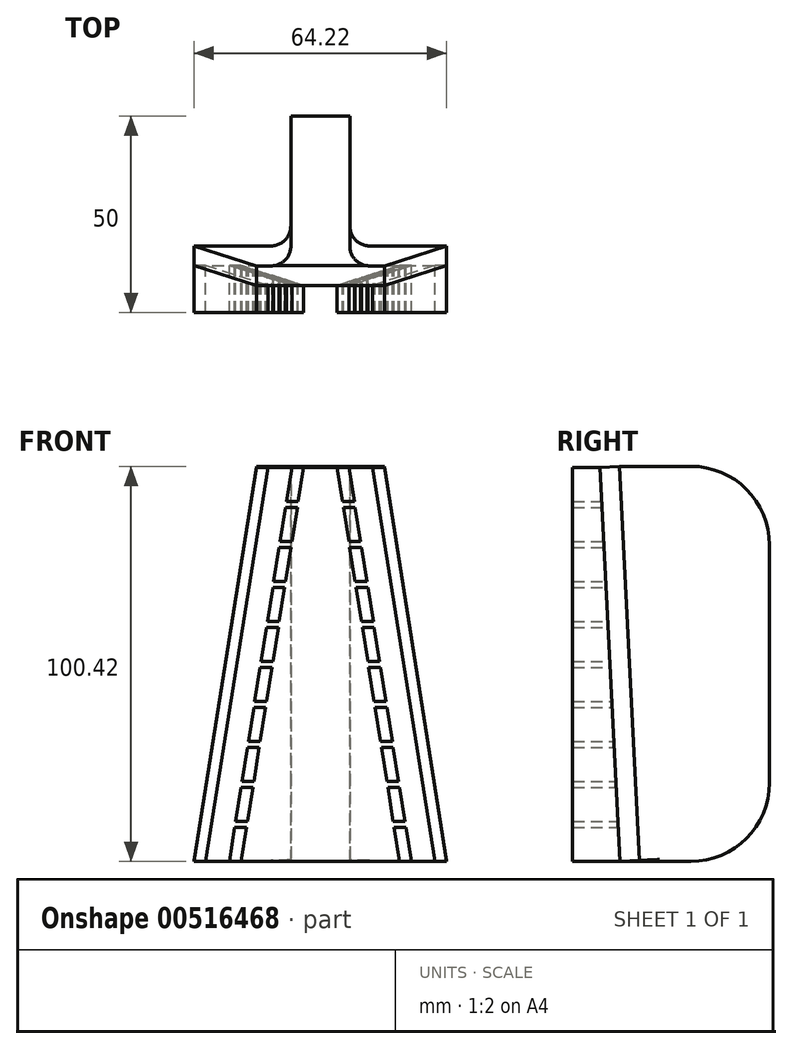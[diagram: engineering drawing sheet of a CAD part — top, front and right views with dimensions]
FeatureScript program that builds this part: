
annotation { "Feature Type Name" : "Feature", "Feature Type Description" : "" }
export const myFeature = defineFeature(function(context is Context, id is Id, definition is map)
    precondition{}
    {
        {
            var Q0;
            Q0=qCreatedBy(makeId("Front.planeOp"),FACE);
            var sketch = newSketch(context, id + "F0", { "sketchPlane" : qUnion([Q0])});
            skLineSegment(sketch, "E0", {"start": v(-21.74, 8.67) * mm, "end": v(-18.74, 8.67) * mm});
            skLineSegment(sketch, "E1", {"start": v(-18.74, 8.67) * mm, "end": v(-20.11, 0) * mm});
            skLineSegment(sketch, "E2", {"start": v(-20.11, 0) * mm, "end": v(-23.11, 0) * mm});
            skLineSegment(sketch, "E3", {"start": v(-23.11, 0) * mm, "end": v(-21.74, 8.67) * mm});
            skLineSegment(sketch, "E4", {"start": v(18.74, 8.67) * mm, "end": v(21.74, 8.67) * mm});
            skLineSegment(sketch, "E5", {"start": v(21.74, 8.67) * mm, "end": v(23.11, 0) * mm});
            skLineSegment(sketch, "E6", {"start": v(23.11, 0) * mm, "end": v(20.11, 0) * mm});
            skLineSegment(sketch, "E7", {"start": v(20.11, 0) * mm, "end": v(18.74, 8.67) * mm});
            skLineSegment(sketch, "E8", {"start": v(-21.5, 10.17) * mm, "end": v(-18.5, 10.17) * mm});
            skLineSegment(sketch, "E9", {"start": v(-18.5, 10.17) * mm, "end": v(-17.13, 18.83) * mm});
            skLineSegment(sketch, "E10", {"start": v(-17.13, 18.83) * mm, "end": v(-20.13, 18.83) * mm});
            skLineSegment(sketch, "E11", {"start": v(-20.13, 18.83) * mm, "end": v(-21.5, 10.17) * mm});
            skLineSegment(sketch, "E12", {"start": v(18.5, 10.17) * mm, "end": v(17.13, 18.83) * mm});
            skLineSegment(sketch, "E13", {"start": v(17.13, 18.83) * mm, "end": v(20.13, 18.83) * mm});
            skLineSegment(sketch, "E14", {"start": v(20.13, 18.83) * mm, "end": v(21.5, 10.17) * mm});
            skLineSegment(sketch, "E15", {"start": v(21.5, 10.17) * mm, "end": v(18.5, 10.17) * mm});
            skLineSegment(sketch, "E16", {"start": v(-18.52, 29) * mm, "end": v(-19.89, 20.33) * mm});
            skLineSegment(sketch, "E17", {"start": v(-19.89, 20.33) * mm, "end": v(-16.89, 20.33) * mm});
            skLineSegment(sketch, "E18", {"start": v(-16.89, 20.33) * mm, "end": v(-15.52, 29) * mm});
            skLineSegment(sketch, "E19", {"start": v(-15.52, 29) * mm, "end": v(-18.52, 29) * mm});
            skLineSegment(sketch, "E20", {"start": v(19.89, 20.33) * mm, "end": v(18.52, 29) * mm});
            skLineSegment(sketch, "E21", {"start": v(18.52, 29) * mm, "end": v(15.52, 29) * mm});
            skLineSegment(sketch, "E22", {"start": v(15.52, 29) * mm, "end": v(16.89, 20.33) * mm});
            skLineSegment(sketch, "E23", {"start": v(16.89, 20.33) * mm, "end": v(19.89, 20.33) * mm});
            skLineSegment(sketch, "E24", {"start": v(-16.67, 40.67) * mm, "end": v(-13.67, 40.67) * mm});
            skLineSegment(sketch, "E25", {"start": v(-13.67, 40.67) * mm, "end": v(-12.3, 49.33) * mm});
            skLineSegment(sketch, "E26", {"start": v(-12.3, 49.33) * mm, "end": v(-15.3, 49.33) * mm});
            skLineSegment(sketch, "E27", {"start": v(-15.3, 49.33) * mm, "end": v(-16.67, 40.67) * mm});
            skLineSegment(sketch, "E28", {"start": v(-13.69, 59.5) * mm, "end": v(-15.06, 50.83) * mm});
            skLineSegment(sketch, "E29", {"start": v(-8.84, 71.17) * mm, "end": v(-11.84, 71.17) * mm});
            skLineSegment(sketch, "E30", {"start": v(-7.47, 79.83) * mm, "end": v(-10.47, 79.83) * mm});
            skLineSegment(sketch, "E31", {"start": v(-10.47, 79.83) * mm, "end": v(-11.84, 71.17) * mm});
            skLineSegment(sketch, "E32", {"start": v(-8.86, 90) * mm, "end": v(-10.23, 81.33) * mm});
            skLineSegment(sketch, "E33", {"start": v(-10.23, 81.33) * mm, "end": v(-7.23, 81.33) * mm});
            skLineSegment(sketch, "E34", {"start": v(-7.23, 81.33) * mm, "end": v(-5.86, 90) * mm});
            skLineSegment(sketch, "E35", {"start": v(-5.86, 90) * mm, "end": v(-8.86, 90) * mm});
            skLineSegment(sketch, "E36", {"start": v(-7.25, 100.17) * mm, "end": v(-8.62, 91.5) * mm});
            skLineSegment(sketch, "E37", {"start": v(-8.62, 91.5) * mm, "end": v(-5.62, 91.5) * mm});
            skLineSegment(sketch, "E38", {"start": v(-5.62, 91.5) * mm, "end": v(-4.25, 100.17) * mm});
            skLineSegment(sketch, "E39", {"start": v(-7.25, 100.17) * mm, "end": v(-4.25, 100.17) * mm});
            skLineSegment(sketch, "E40", {"start": v(13.9, 39.17) * mm, "end": v(16.9, 39.17) * mm});
            skLineSegment(sketch, "E41", {"start": v(16.9, 39.17) * mm, "end": v(18.28, 30.5) * mm});
            skLineSegment(sketch, "E42", {"start": v(18.28, 30.5) * mm, "end": v(15.28, 30.5) * mm});
            skLineSegment(sketch, "E43", {"start": v(15.28, 30.5) * mm, "end": v(13.9, 39.17) * mm});
            skLineSegment(sketch, "E44", {"start": v(12.3, 49.33) * mm, "end": v(15.3, 49.33) * mm});
            skLineSegment(sketch, "E45", {"start": v(15.3, 49.33) * mm, "end": v(16.67, 40.67) * mm});
            skLineSegment(sketch, "E46", {"start": v(16.67, 40.67) * mm, "end": v(13.67, 40.67) * mm});
            skLineSegment(sketch, "E47", {"start": v(13.67, 40.67) * mm, "end": v(12.3, 49.33) * mm});
            skLineSegment(sketch, "E48", {"start": v(10.69, 59.5) * mm, "end": v(13.69, 59.5) * mm});
            skLineSegment(sketch, "E49", {"start": v(13.69, 59.5) * mm, "end": v(15.06, 50.83) * mm});
            skLineSegment(sketch, "E50", {"start": v(15.06, 50.83) * mm, "end": v(12.06, 50.83) * mm});
            skLineSegment(sketch, "E51", {"start": v(12.06, 50.83) * mm, "end": v(10.69, 59.5) * mm});
            skLineSegment(sketch, "E52", {"start": v(13.45, 61) * mm, "end": v(10.45, 61) * mm});
            skLineSegment(sketch, "E53", {"start": v(7.47, 79.83) * mm, "end": v(10.47, 79.83) * mm});
            skLineSegment(sketch, "E54", {"start": v(10.47, 79.83) * mm, "end": v(11.84, 71.17) * mm});
            skLineSegment(sketch, "E55", {"start": v(11.84, 71.17) * mm, "end": v(8.84, 71.17) * mm});
            skLineSegment(sketch, "E56", {"start": v(8.84, 71.17) * mm, "end": v(7.47, 79.83) * mm});
            skLineSegment(sketch, "E57", {"start": v(5.86, 90) * mm, "end": v(8.86, 90) * mm});
            skLineSegment(sketch, "E58", {"start": v(8.86, 90) * mm, "end": v(10.23, 81.33) * mm});
            skLineSegment(sketch, "E59", {"start": v(10.23, 81.33) * mm, "end": v(7.23, 81.33) * mm});
            skLineSegment(sketch, "E60", {"start": v(7.23, 81.33) * mm, "end": v(5.86, 90) * mm});
            skLineSegment(sketch, "E61", {"start": v(-23.11, 192.36) * mm, "end": v(-23.11, -60.17) * mm, "construction": true});
            skLineSegment(sketch, "E62", {"start": v(-16.9, 39.17) * mm, "end": v(-18.28, 30.5) * mm});
            skLineSegment(sketch, "E63", {"start": v(-18.28, 30.5) * mm, "end": v(-15.28, 30.5) * mm});
            skLineSegment(sketch, "E64", {"start": v(-15.28, 30.5) * mm, "end": v(-13.9, 39.17) * mm});
            skLineSegment(sketch, "E65", {"start": v(-13.9, 39.17) * mm, "end": v(-16.9, 39.17) * mm});
            skLineSegment(sketch, "E66", {"start": v(23.11, 282.2) * mm, "end": v(23.11, 74.17) * mm, "construction": true});
            skLineSegment(sketch, "E67", {"start": v(-18.5, 10.17) * mm, "end": v(18.5, 10.17) * mm, "construction": true});
            skLineSegment(sketch, "E68", {"start": v(-20.11, 0) * mm, "end": v(20.11, 0) * mm, "construction": true});
            skLineSegment(sketch, "E69", {"start": v(-18.74, 8.67) * mm, "end": v(18.74, 8.67) * mm, "construction": true});
            skLineSegment(sketch, "E70", {"start": v(-17.13, 18.83) * mm, "end": v(17.13, 18.83) * mm, "construction": true});
            skLineSegment(sketch, "E71", {"start": v(-16.89, 20.33) * mm, "end": v(16.89, 20.33) * mm, "construction": true});
            skLineSegment(sketch, "E72", {"start": v(-15.52, 29) * mm, "end": v(15.52, 29) * mm, "construction": true});
            skLineSegment(sketch, "E73", {"start": v(-15.28, 30.5) * mm, "end": v(15.28, 30.5) * mm, "construction": true});
            skLineSegment(sketch, "E74", {"start": v(-13.9, 39.17) * mm, "end": v(13.9, 39.17) * mm, "construction": true});
            skLineSegment(sketch, "E75", {"start": v(-13.67, 40.67) * mm, "end": v(13.67, 40.67) * mm, "construction": true});
            skLineSegment(sketch, "E76", {"start": v(-12.3, 49.33) * mm, "end": v(12.3, 49.33) * mm, "construction": true});
            skLineSegment(sketch, "E77", {"start": v(-7.47, 79.83) * mm, "end": v(7.47, 79.83) * mm, "construction": true});
            skLineSegment(sketch, "E78", {"start": v(-7.23, 81.33) * mm, "end": v(7.23, 81.33) * mm, "construction": true});
            skLineSegment(sketch, "E79", {"start": v(-5.86, 90) * mm, "end": v(5.86, 90) * mm, "construction": true});
            skLineSegment(sketch, "E80", {"start": v(-5.62, 91.5) * mm, "end": v(5.62, 91.5) * mm, "construction": true});
            skLineSegment(sketch, "E81", {"start": v(-4.25, 100.17) * mm, "end": v(4.25, 100.17) * mm, "construction": true});
            skLineSegment(sketch, "E82", {"start": v(-21.74, 8.67) * mm, "end": v(-21.5, 10.17) * mm, "construction": true});
            skLineSegment(sketch, "E83", {"start": v(-20.13, 18.83) * mm, "end": v(-19.89, 20.33) * mm, "construction": true});
            skLineSegment(sketch, "E84", {"start": v(-18.52, 29) * mm, "end": v(-18.28, 30.5) * mm, "construction": true});
            skLineSegment(sketch, "E85", {"start": v(-16.9, 39.17) * mm, "end": v(-16.67, 40.67) * mm, "construction": true});
            skLineSegment(sketch, "E86", {"start": v(-15.3, 49.33) * mm, "end": v(-15.06, 50.83) * mm, "construction": true});
            skLineSegment(sketch, "E87", {"start": v(-13.69, 59.5) * mm, "end": v(-13.45, 61) * mm, "construction": true});
            skLineSegment(sketch, "E88", {"start": v(-11.84, 71.17) * mm, "end": v(-11.84, 71.17) * mm});
            skLineSegment(sketch, "E89", {"start": v(-10.23, 81.33) * mm, "end": v(-10.47, 79.83) * mm, "construction": true});
            skLineSegment(sketch, "E90", {"start": v(-8.86, 90) * mm, "end": v(-8.62, 91.5) * mm, "construction": true});
            skLineSegment(sketch, "E91", {"start": v(-13.69, 59.5) * mm, "end": v(-10.69, 59.5) * mm});
            skLineSegment(sketch, "E92", {"start": v(-10.69, 59.5) * mm, "end": v(-12.06, 50.83) * mm});
            skLineSegment(sketch, "E93", {"start": v(-12.06, 50.83) * mm, "end": v(-15.06, 50.83) * mm});
            skLineSegment(sketch, "E94", {"start": v(-10.69, 59.5) * mm, "end": v(10.69, 59.5) * mm, "construction": true});
            skLineSegment(sketch, "E95", {"start": v(-12.06, 50.83) * mm, "end": v(12.06, 50.83) * mm, "construction": true});
            skLineSegment(sketch, "E96", {"start": v(-18.74, 8.67) * mm, "end": v(-18.5, 10.17) * mm, "construction": true});
            skLineSegment(sketch, "E97", {"start": v(-17.13, 18.83) * mm, "end": v(-16.89, 20.33) * mm, "construction": true});
            skLineSegment(sketch, "E98", {"start": v(-15.52, 29) * mm, "end": v(-15.28, 30.5) * mm, "construction": true});
            skLineSegment(sketch, "E99", {"start": v(-13.9, 39.17) * mm, "end": v(-13.67, 40.67) * mm, "construction": true});
            skLineSegment(sketch, "E100", {"start": v(-12.3, 49.33) * mm, "end": v(-12.06, 50.83) * mm, "construction": true});
            skLineSegment(sketch, "E101", {"start": v(-8.84, 71.17) * mm, "end": v(8.84, 71.17) * mm, "construction": true});
            skLineSegment(sketch, "E102", {"start": v(-13.45, 61) * mm, "end": v(-12.08, 69.67) * mm});
            skLineSegment(sketch, "E103", {"start": v(13.45, 61) * mm, "end": v(12.08, 69.67) * mm});
            skLineSegment(sketch, "E104", {"start": v(12.08, 69.67) * mm, "end": v(9.08, 69.67) * mm});
            skLineSegment(sketch, "E105", {"start": v(9.08, 69.67) * mm, "end": v(10.45, 61) * mm});
            skLineSegment(sketch, "E106", {"start": v(-7.47, 79.83) * mm, "end": v(-7.23, 81.33) * mm, "construction": true});
            skLineSegment(sketch, "E107", {"start": v(-5.86, 90) * mm, "end": v(-5.62, 91.5) * mm, "construction": true});
            skLineSegment(sketch, "E108", {"start": v(-12.08, 69.67) * mm, "end": v(-9.08, 69.67) * mm});
            skLineSegment(sketch, "E109", {"start": v(-9.08, 69.67) * mm, "end": v(-10.45, 61) * mm});
            skLineSegment(sketch, "E110", {"start": v(-10.45, 61) * mm, "end": v(-13.45, 61) * mm});
            skLineSegment(sketch, "E111", {"start": v(-12.08, 69.67) * mm, "end": v(-11.84, 71.17) * mm, "construction": true});
            skLineSegment(sketch, "E112", {"start": v(-8.84, 71.17) * mm, "end": v(-9.08, 69.67) * mm, "construction": true});
            skLineSegment(sketch, "E113", {"start": v(-10.45, 61) * mm, "end": v(-10.69, 59.5) * mm, "construction": true});
            skLineSegment(sketch, "E114", {"start": v(-7.47, 79.83) * mm, "end": v(-8.84, 71.17) * mm});
            skLineSegment(sketch, "E115", {"start": v(-9.08, 69.67) * mm, "end": v(9.08, 69.67) * mm, "construction": true});
            skLineSegment(sketch, "E116", {"start": v(-10.45, 61) * mm, "end": v(10.45, 61) * mm, "construction": true});
            skLineSegment(sketch, "E117", {"start": v(15.52, 29) * mm, "end": v(15.28, 30.5) * mm, "construction": true});
            skLineSegment(sketch, "E118", {"start": v(18.28, 30.5) * mm, "end": v(18.52, 29) * mm, "construction": true});
            skLineSegment(sketch, "E119", {"start": v(16.67, 40.67) * mm, "end": v(16.9, 39.17) * mm, "construction": true});
            skLineSegment(sketch, "E120", {"start": v(13.67, 40.67) * mm, "end": v(13.9, 39.17) * mm, "construction": true});
            skLineSegment(sketch, "E121", {"start": v(20.13, 18.83) * mm, "end": v(19.89, 20.33) * mm, "construction": true});
            skLineSegment(sketch, "E122", {"start": v(17.13, 18.83) * mm, "end": v(16.89, 20.33) * mm, "construction": true});
            skLineSegment(sketch, "E123", {"start": v(10.23, 81.33) * mm, "end": v(10.47, 79.83) * mm, "construction": true});
            skLineSegment(sketch, "E124", {"start": v(12.08, 69.67) * mm, "end": v(11.84, 71.17) * mm, "construction": true});
            skLineSegment(sketch, "E125", {"start": v(13.45, 61) * mm, "end": v(13.69, 59.5) * mm, "construction": true});
            skLineSegment(sketch, "E126", {"start": v(10.69, 59.5) * mm, "end": v(10.45, 61) * mm, "construction": true});
            skLineSegment(sketch, "E127", {"start": v(9.08, 69.67) * mm, "end": v(8.84, 71.17) * mm, "construction": true});
            skLineSegment(sketch, "E128", {"start": v(7.47, 79.83) * mm, "end": v(7.23, 81.33) * mm, "construction": true});
            skLineSegment(sketch, "E129", {"start": v(5.86, 90) * mm, "end": v(5.62, 91.5) * mm, "construction": true});
            skLineSegment(sketch, "E130", {"start": v(12.06, 50.83) * mm, "end": v(12.3, 49.33) * mm, "construction": true});
            skLineSegment(sketch, "E131", {"start": v(15.3, 49.33) * mm, "end": v(15.06, 50.83) * mm, "construction": true});
            skLineSegment(sketch, "E132", {"start": v(18.5, 10.17) * mm, "end": v(18.74, 8.67) * mm, "construction": true});
            skLineSegment(sketch, "E133", {"start": v(21.5, 10.17) * mm, "end": v(21.74, 8.67) * mm, "construction": true});
            skLineSegment(sketch, "E134", {"start": v(4.25, 100.17) * mm, "end": v(5.62, 91.5) * mm});
            skLineSegment(sketch, "E135", {"start": v(5.62, 91.5) * mm, "end": v(8.62, 91.5) * mm});
            skLineSegment(sketch, "E136", {"start": v(8.62, 91.5) * mm, "end": v(7.25, 100.17) * mm});
            skLineSegment(sketch, "E137", {"start": v(7.25, 100.17) * mm, "end": v(4.25, 100.17) * mm});
            skLineSegment(sketch, "E138", {"start": v(8.62, 91.5) * mm, "end": v(8.86, 90) * mm, "construction": true});
            skLineSegment(sketch, "E139", {"start": v(28.76, 100.17) * mm, "end": v(28.76, 91.5) * mm, "construction": true});
            skLineSegment(sketch, "E140", {"start": v(17.63, 90) * mm, "end": v(17.63, 81.33) * mm, "construction": true});
            skLineSegment(sketch, "E141", {"start": v(16.71, 79.83) * mm, "end": v(16.71, 71.17) * mm, "construction": true});
            skLineSegment(sketch, "E142", {"start": v(15.8, 69.67) * mm, "end": v(15.8, 61) * mm, "construction": true});
            skLineSegment(sketch, "E143", {"start": v(11.38, 59.5) * mm, "end": v(11.38, 50.83) * mm, "construction": true});
            skLineSegment(sketch, "E144", {"start": v(10.77, 49.33) * mm, "end": v(10.77, 40.67) * mm, "construction": true});
            skLineSegment(sketch, "E145", {"start": v(10, 39.17) * mm, "end": v(10, 30.5) * mm, "construction": true});
            skLineSegment(sketch, "E146", {"start": v(8.32, 29) * mm, "end": v(8.32, 20.33) * mm, "construction": true});
            skLineSegment(sketch, "E147", {"start": v(10.15, 18.83) * mm, "end": v(10.15, 10.17) * mm, "construction": true});
            skLineSegment(sketch, "E148", {"start": v(-201.28, 8.67) * mm, "end": v(-201.28, 0) * mm, "construction": true});
            skLineSegment(sketch, "E149", {"start": v(105.4, 8.67) * mm, "end": v(105.4, 10.17) * mm, "construction": true});
            skLineSegment(sketch, "E150", {"start": v(103.22, 18.83) * mm, "end": v(103.22, 20.33) * mm, "construction": true});
            skLineSegment(sketch, "E151", {"start": v(107.03, 29) * mm, "end": v(107.03, 30.5) * mm, "construction": true});
            skLineSegment(sketch, "E152", {"start": v(99.41, 39.17) * mm, "end": v(99.41, 40.67) * mm, "construction": true});
            skLineSegment(sketch, "E153", {"start": v(105.4, 49.33) * mm, "end": v(105.4, 50.83) * mm, "construction": true});
            skLineSegment(sketch, "E154", {"start": v(95.24, 59.5) * mm, "end": v(95.24, 61) * mm, "construction": true});
            skLineSegment(sketch, "E155", {"start": v(103.58, 69.67) * mm, "end": v(103.58, 71.17) * mm, "construction": true});
            skLineSegment(sketch, "E156", {"start": v(88.35, 79.83) * mm, "end": v(88.35, 81.33) * mm, "construction": true});
            skLineSegment(sketch, "E157", {"start": v(99.05, 90) * mm, "end": v(99.05, 91.5) * mm, "construction": true});
            skLineSegment(sketch, "E158", {"start": v(-13.25, 100.17) * mm, "end": v(-29.11, 0) * mm});
            skLineSegment(sketch, "E159", {"start": v(-29.11, 0) * mm, "end": v(-32.11, 0) * mm});
            skLineSegment(sketch, "E160", {"start": v(-32.11, 0) * mm, "end": v(-16.25, 100.17) * mm});
            skLineSegment(sketch, "E161", {"start": v(-16.25, 100.17) * mm, "end": v(-13.25, 100.17) * mm});
            skLineSegment(sketch, "E162", {"start": v(13.25, 100.17) * mm, "end": v(16.25, 100.17) * mm});
            skLineSegment(sketch, "E163", {"start": v(16.25, 100.17) * mm, "end": v(32.11, 0) * mm});
            skLineSegment(sketch, "E164", {"start": v(32.11, 0) * mm, "end": v(29.11, 0) * mm});
            skLineSegment(sketch, "E165", {"start": v(29.11, 0) * mm, "end": v(13.25, 100.17) * mm});
            skLineSegment(sketch, "E166", {"start": v(-13.25, 100.17) * mm, "end": v(-7.25, 100.17) * mm, "construction": true});
            skLineSegment(sketch, "E167", {"start": v(7.25, 100.17) * mm, "end": v(13.25, 100.17) * mm, "construction": true});
            skLineSegment(sketch, "E168", {"start": v(-29.11, 0) * mm, "end": v(-23.11, 0) * mm, "construction": true});
            skLineSegment(sketch, "E169", {"start": v(23.11, 0) * mm, "end": v(29.11, 0) * mm, "construction": true});
            skSolve(sketch);
        }
        {
            var Q0;
            Q0 = qSketchRegion(id + "F0", true);
            extrude(context, id + "F1", {"entities" : qUnion([Q0]), "depth" : 12 * mm, "offsetDistance" : 25 * mm});
        }
        {
            var Q0;
            Q0=qCreatedBy(makeId("Right.planeOp"),FACE);
            var sketch = newSketch(context, id + "F2", { "sketchPlane" : qUnion([Q0])});
            skLineSegment(sketch, "E170", {"start": v(0, 0) * mm, "end": v(-5.07, 100.17) * mm});
            skLineSegment(sketch, "E171", {"start": v(-5.07, 100.17) * mm, "end": v(0, 100.17) * mm});
            skLineSegment(sketch, "E172", {"start": v(0, 100.17) * mm, "end": v(0, 0) * mm});
            skSolve(sketch);
        }
        {
            var Q0;
            Q0 = qSketchRegion(id + "F2", true);
            extrude(context, id + "F3", {"entities" : qUnion([Q0]), "operationType" : NewBodyOperationType.REMOVE, "depth" : 80 * mm, "offsetDistance" : 25 * mm, "symmetric" : true});
        }
        {
            var Q0;
            Q0=makeQuery(id+"F3.boolean.opBoolean","COPY",FACE,{"disambiguationData":[TD([makeQuery(id+"F1.opExtrude","SWEPT_FACE",FACE,{"disambiguationData":[OSD([sQuery(id+"F0.wireOp",EDGE,"E162")])]})])],"derivedFrom":makeQuery(id+"F3.opExtrude","SWEPT_FACE",FACE,{"disambiguationData":[OSD([sQuery(id+"F2.wireOp",EDGE,"E170")])]})});
            var sketch = newSketch(context, id + "F4", { "sketchPlane" : qUnion([Q0])});
            skLineSegment(sketch, "E173", {"start": v(-16.25, 100.3) * mm, "end": v(16.25, 100.3) * mm});
            skLineSegment(sketch, "E174", {"start": v(16.25, 100.3) * mm, "end": v(32.11, 0) * mm});
            skLineSegment(sketch, "E175", {"start": v(32.11, 0) * mm, "end": v(-32.11, 0) * mm});
            skLineSegment(sketch, "E176", {"start": v(-32.11, 0) * mm, "end": v(-16.25, 100.3) * mm});
            skSolve(sketch);
        }
        {
            var Q0;
            Q0 = qSketchRegion(id + "F4", true);
            extrude(context, id + "F5", {"entities" : qUnion([Q0]), "depth" : 5 * mm, "offsetDistance" : 25 * mm});
        }
        {
            var Q0;
            Q0=qCreatedBy(makeId("Right.planeOp"),FACE);
            var sketch = newSketch(context, id + "F6", { "sketchPlane" : qUnion([Q0])});
            skLineSegment(sketch, "E177.bottom", {"start": v(0, 0) * mm, "end": v(38, 0) * mm});
            skLineSegment(sketch, "E177.top", {"start": v(0, 100.42) * mm, "end": v(38, 100.42) * mm});
            skLineSegment(sketch, "E177.left", {"start": v(0, 0) * mm, "end": v(0, 100.42) * mm});
            skLineSegment(sketch, "E177.right", {"start": v(38, 0) * mm, "end": v(38, 100.42) * mm});
            skSolve(sketch);
        }
        {
            var Q0;
            Q0 = qSketchRegion(id + "F6", true);
            extrude(context, id + "F7", {"entities" : qUnion([Q0]), "operationType" : NewBodyOperationType.ADD, "depth" : 15 * mm, "offsetDistance" : 25 * mm, "symmetric" : true});
        }
        {
            var Q0;
            Q0=qCreatedBy(makeId("Right.planeOp"),FACE);
            var sketch = newSketch(context, id + "F8", { "sketchPlane" : qUnion([Q0])});
            skLineSegment(sketch, "E178", {"start": v(0, 100.42) * mm, "end": v(0.72, 99.84) * mm});
            skLineSegment(sketch, "E179", {"start": v(0.72, 99.84) * mm, "end": v(-0.17, 98.34) * mm});
            skLineSegment(sketch, "E180", {"start": v(-0.17, 98.34) * mm, "end": v(-0.43, 99.98) * mm});
            skLineSegment(sketch, "E181", {"start": v(-0.43, 99.98) * mm, "end": v(-0.08, 100.42) * mm});
            skLineSegment(sketch, "E182", {"start": v(-0.08, 100.42) * mm, "end": v(0, 100.42) * mm});
            skSolve(sketch);
        }
        {
            var Q0;
            Q0 = qSketchRegion(id + "F8", true);
            extrude(context, id + "F9", {"entities" : qUnion([Q0]), "operationType" : NewBodyOperationType.ADD, "depth" : 15 * mm, "offsetDistance" : 25 * mm, "symmetric" : true});
        }
        {
            var Q0;
            Q0=makeQuery(id+"F9.boolean.opBoolean","INTERSECT",EDGE,{"derivedFrom":[makeQuery(id+"F5.opExtrude","CAP_FACE",FACE,{"disambiguationData":[OSD([sQuery(id+"F4.wireOp",EDGE,"E173"),sQuery(id+"F4.wireOp",EDGE,"E174"),sQuery(id+"F4.wireOp",EDGE,"E175"),sQuery(id+"F4.wireOp",EDGE,"E176")])],"isStart":false}),makeQuery(id+"F9.opExtrude","CAP_FACE",FACE,{"disambiguationData":[OSD([sQuery(id+"F8.wireOp",EDGE,"E178"),sQuery(id+"F8.wireOp",EDGE,"E179"),sQuery(id+"F8.wireOp",EDGE,"E180"),sQuery(id+"F8.wireOp",EDGE,"E181"),sQuery(id+"F8.wireOp",EDGE,"E182")])],"isStart":false})]});
            var Q1;
            Q1=makeQuery(id+"F9.boolean.opBoolean","INTERSECT",EDGE,{"derivedFrom":[makeQuery(id+"F5.opExtrude","CAP_FACE",FACE,{"disambiguationData":[OSD([sQuery(id+"F4.wireOp",EDGE,"E173"),sQuery(id+"F4.wireOp",EDGE,"E174"),sQuery(id+"F4.wireOp",EDGE,"E175"),sQuery(id+"F4.wireOp",EDGE,"E176")])],"isStart":false}),makeQuery(id+"F9.opExtrude","CAP_FACE",FACE,{"disambiguationData":[OSD([sQuery(id+"F8.wireOp",EDGE,"E178"),sQuery(id+"F8.wireOp",EDGE,"E179"),sQuery(id+"F8.wireOp",EDGE,"E180"),sQuery(id+"F8.wireOp",EDGE,"E181"),sQuery(id+"F8.wireOp",EDGE,"E182")])],"isStart":true})]});
            fillet(context, id + "F10", {"entities" : qUnion([Q0, Q1]), "radius" : 5 * mm, "tangentPropagation" : true, "allowEdgeOverflow" : false});
        }
        {
            var Q0;
            Q0=makeQuery(id+"F7.opExtrude","SWEPT_EDGE",EDGE,{"disambiguationData":[OSD([sQuery(id+"F6.wireOp",EDGE,"E177.top"),sQuery(id+"F6.wireOp",EDGE,"E177.right")])]});
            var Q1;
            Q1=makeQuery(id+"F7.opExtrude","SWEPT_EDGE",EDGE,{"disambiguationData":[OSD([sQuery(id+"F6.wireOp",EDGE,"E177.bottom"),sQuery(id+"F6.wireOp",EDGE,"E177.right")])]});
            fillet(context, id + "F11", {"entities" : qUnion([Q0, Q1]), "radius" : 20 * mm, "tangentPropagation" : true, "allowEdgeOverflow" : false});
        }
    });
